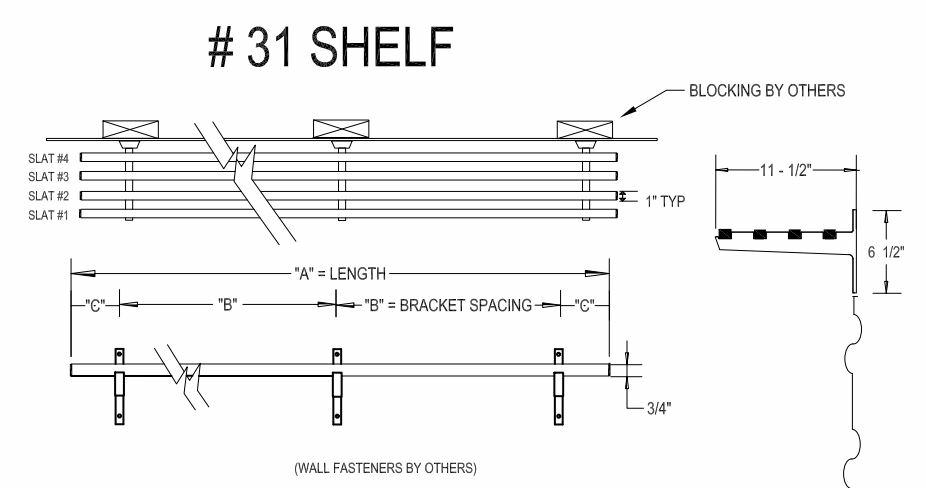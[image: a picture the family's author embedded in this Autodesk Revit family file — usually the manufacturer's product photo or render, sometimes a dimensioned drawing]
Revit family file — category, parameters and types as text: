
# Revit family: HookSystem_W_EMCO
name_source: partatom
category: Generic Models
units: mm (PartAtom-declared; Revit-internal decimal feet)

## family parameters
Always vertical = Yes
Can host rebar = No
Cut with Voids When Loaded = No
Maintain Annotation Orientation = No
Part Type = Normal
Room Calculation Point = No
Round Connector Dimension = Use Diameter
Shared = No
Work Plane-Based = Yes

## types (1)
- HookSystem_W_EMCO
    Assembly Code = E1090900
    Construction Details = http://www.emcospi.com
    Default Elevation = 4' - 0"
    Description = EMCO_W Hook Strip System
    Hook Array = 6
    Hook Count = 6
    Hook Material = EMCO_Purple 10HK Hook
    Installation Phase = Closet and Utiity Shelving Hardware
    Installation-Fabrication = http://www.emcospi.com
    Keynote = 10 57 33
    Manufacturer = EMCO Specialty Products, Inc.
    Manufacturer Fax = 913-281-4554
    Manufacturer Website = http://www.emcospi.com
    Model = EMCO_W Hook Strip System
    Product Data = http://www.emcospi.com
    Product Properties = http://www.emcospi.com
    Sales Information = http://www.emcospi.com
    Send Message = http://www.emcospi.com
    Shelf Overhang = 0' - 1"
    Slat Material = EMCO_Silver Anodized Aluminum
    Specification = http://www.emcospi.com
    URL = https://www.arcat.com
    Unit Length = 3' - 0"
    Wall Channel Count = 2
    Warranty Duration (Years) = 1

## geometry (parser evidence)
native form markers: Sweep x8
no freeform markers — native parametric forms only
